# Revit family: Plumbing-Showerheads-Sloan-Valve-AC-51z
name_source: partatom
category: Plumbing Fixtures
units: mm (PartAtom-declared; Revit-internal decimal feet)

## family parameters
Cut with Voids When Loaded = No
Host = Face
OmniClass Number = 23.40.20.21
OmniClass Title = Toilet and Bath Specialties
Part Type = Normal
Room Calculation Point = No
Round Connector Dimension = Use Diameter
Shared = No

## types (10) — shared parameters
Assembly Code = D2010
Default Elevation = 8"
Depth = 2 1/2"
Edition number = 1
Height = 3 5/8"
Keynote = 15410
Manufacturer = Sloan Valve
Product data url = https://bimobject.com
URL = www.sloanvalve.com
Water Inlet Connection Diameter = 1"
Width = 2 1/2"

## per-type parameters (varying)
| type | Description | Model | Part Number | Product Material | Water Flow |
| AC-51-1.8GPM-CP | Polished Chrome Finish, Act-O-Matic® Standard Showerhead. | AC-51-1.8GPM-CP | 4021031 | Sloan Valve - Finish - Polished Chrome | 2 GPM |
| AC-51-2.0GPM-CP -1 | Polished Chrome Finish, Act-O-Matic® Standard Showerhead. | AC-51-2.0GPM-CP | 4021030 | Sloan Valve - Finish - Polished Chrome | 2 GPM |
| AC-51-2.0GPM-CP -2 | Polished Chrome Finish, Act-O-Matic® Standard Showerhead. | AC-51-2.0GPM-CP | 4021050 | Sloan Valve - Finish - Polished Chrome | 2 GPM |
| AC-51-2.0GPM-CP-SH14-VP | Polished Chrome Finish, SH-14 Vandal Proof Ball Joint, Act-O-Matic® Standard Showerhead. | AC-51-2.0GPM-CP-SH14-VP | 4021040 | Sloan Valve - Finish - Polished Chrome | 2 GPM |
| AC-51-2.5GPM-BN | Brushed Nickel Finish, Act-O-Matic® Standard Showerhead. | AC-51-2.5GPM-BN | 4021002 | Sloan Valve - Finish - Brushed Nickel | 3 GPM |
| AC-51-2.5GPM-CP -1 | Polished Chrome Finish, Act-O-Matic® Standard Showerhead. | AC-51-2.5GPM-CP | 4021000 | Sloan Valve - Finish - Polished Chrome | 3 GPM |
| AC-51-2.5GPM-CP -2 | Polished Chrome Finish, Act-O-Matic® Standard Showerhead. | AC-51-2.5GPM-CP | 4021004 | Sloan Valve - Finish - Polished Chrome | 3 GPM |
| AC-51-2.5GPM-CP-SH14-VP | Polished Chrome Finish, SH-14 Vandal Proof Ball Joint, Act-O-Matic® Standard Showerhead. | AC-51-2.5GPM-CP-SH14-VP | 4021011 | Sloan Valve - Finish - Polished Chrome | 3 GPM |
| AC-51-2.5GPM-PB | Polished Brass Finish, Act-O-Matic® Standard Showerhead. | AC-51-2.5GPM-PB | 4021029 | Sloan Valve - Finish - Polished Brass | 3 GPM |
| AC-51-2.5GPM-SF | Brushed Stainless Finish, Act-O-Matic® Standard Showerhead. | AC-51-2.5GPM-SF | 4021001 | Sloan Valve - Stainless Steel - Brushed | 3 GPM |

## geometry (parser evidence)
native form markers: Sweep x3
no freeform markers — native parametric forms only
